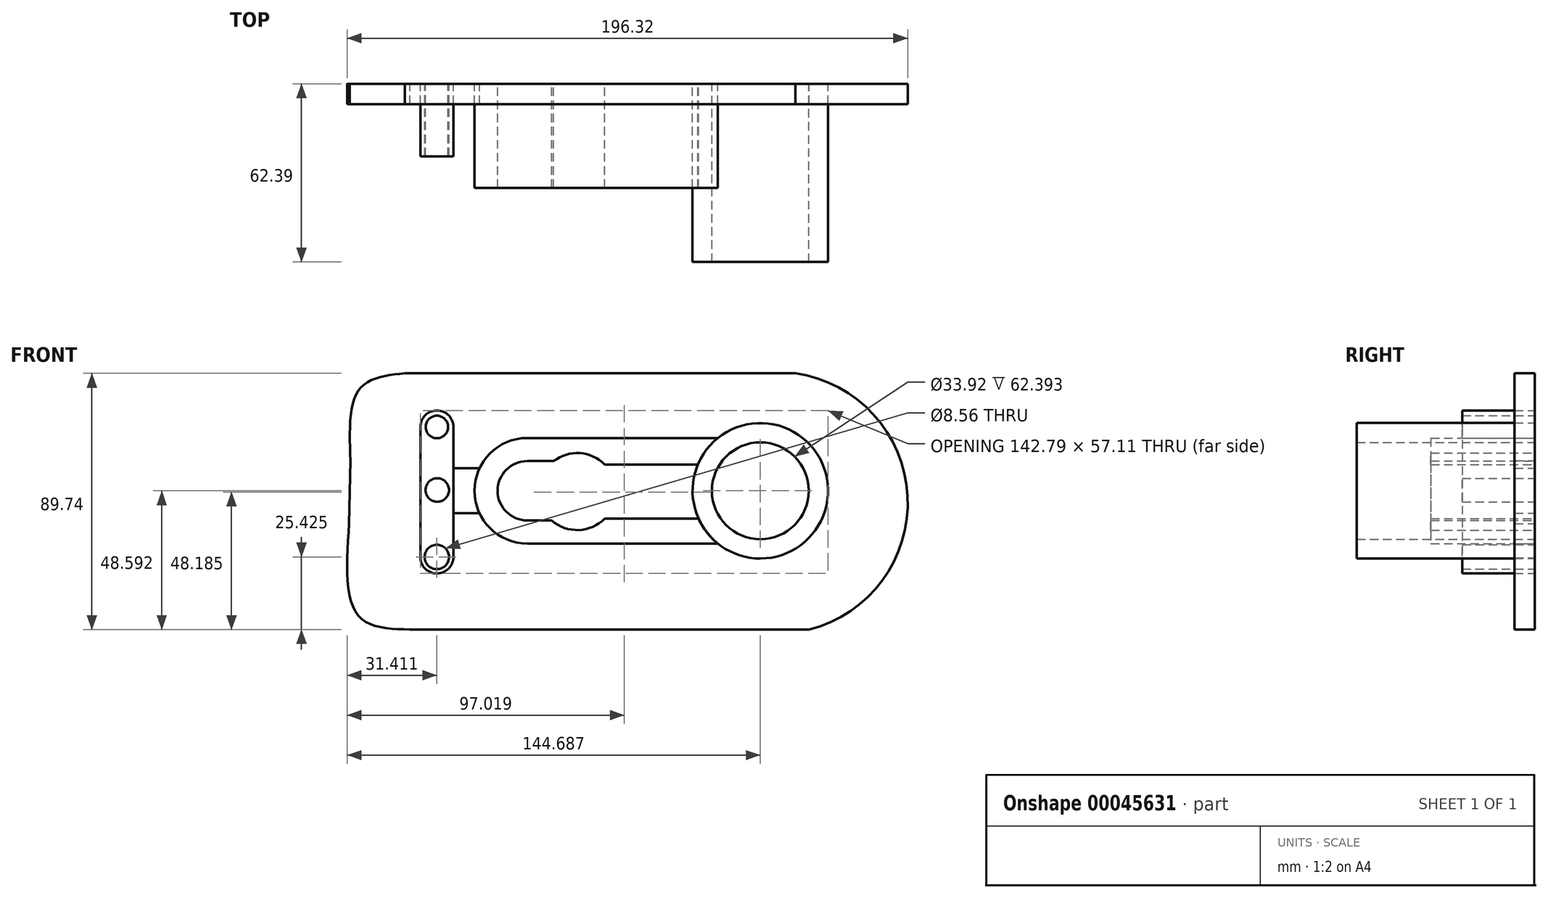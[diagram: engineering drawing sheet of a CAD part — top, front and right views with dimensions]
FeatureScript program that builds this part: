
annotation { "Feature Type Name" : "Feature", "Feature Type Description" : "" }
export const myFeature = defineFeature(function(context is Context, id is Id, definition is map)
    precondition{}
    {
        {
            var Q0;
            Q0=qCreatedBy(makeId("Front.planeOp"),FACE);
            var sketch = newSketch(context, id + "F0", { "sketchPlane" : qUnion([Q0])});
            skLineSegment(sketch, "E0", {"start": v(-64.59, 29) * mm, "end": v(-64.59, -16.8) * mm});
            skArc(sketch, "E1", {"start": v(-64.59, 29) * mm, "mid": v(-58.8, 34.79) * mm, "end": v(-53, 29) * mm});
            skLineSegment(sketch, "E2", {"start": v(-53, 29) * mm, "end": v(-53, -16.52) * mm});
            skArc(sketch, "E3", {"start": v(-53, -16.52) * mm, "mid": v(-58.66, -22.32) * mm, "end": v(-64.59, -16.8) * mm});
            skCircle(sketch, "E4", {"center": v(-58.8, 29) * mm, "radius": 3.93 * mm});
            skCircle(sketch, "E5", {"center": v(-58.8, -16.52) * mm, "radius": 4.28 * mm});
            skCircle(sketch, "E6", {"center": v(54.48, 6.64) * mm, "radius": 23.73 * mm});
            skCircle(sketch, "E7", {"center": v(54.48, 6.64) * mm, "radius": 16.96 * mm});
            skCircle(sketch, "E8", {"center": v(54.48, 6.64) * mm, "radius": 14.65 * mm});
            skLineSegment(sketch, "E9", {"start": v(39.6, 25.12) * mm, "end": v(-27.14, 25.12) * mm});
            skLineSegment(sketch, "E10", {"start": v(39.6, -11.84) * mm, "end": v(-27.14, -11.84) * mm});
            skCircle(sketch, "E11", {"center": v(-9.63, 6.37) * mm, "radius": 13.5 * mm});
            skCircle(sketch, "E12", {"center": v(-9.63, 6.37) * mm, "radius": 9.21 * mm});
            skCircle(sketch, "E13", {"center": v(-9.63, 6.37) * mm, "radius": 7.09 * mm});
            skArc(sketch, "E14", {"start": v(-27.14, 25.12) * mm, "mid": v(-45.62, 6.64) * mm, "end": v(-27.14, -11.84) * mm});
            skLineSegment(sketch, "E15", {"start": v(-17.9, 17.04) * mm, "end": v(-27.14, 17.04) * mm});
            skLineSegment(sketch, "E16", {"start": v(-18.55, -3.75) * mm, "end": v(-27.14, -3.75) * mm});
            skArc(sketch, "E17", {"start": v(-27.14, 17.04) * mm, "mid": v(-37.53, 6.64) * mm, "end": v(-27.14, -3.75) * mm});
            skLineSegment(sketch, "E18", {"start": v(-43.87, 14.51) * mm, "end": v(-53, 14.51) * mm});
            skLineSegment(sketch, "E19", {"start": v(-43.87, -1.23) * mm, "end": v(-53, -1.23) * mm});
            skCircle(sketch, "E20", {"center": v(-58.66, 6.91) * mm, "radius": 4.12 * mm});
            skArc(sketch, "E21", {"start": v(71.62, -41.95) * mm, "mid": v(106.05, 4.9) * mm, "end": v(66.79, 47.8) * mm});
            skLineSegment(sketch, "E22", {"start": v(66.79, 47.8) * mm, "end": v(-70, 47.8) * mm});
            skLineSegment(sketch, "E23", {"start": v(71.62, -41.95) * mm, "end": v(-68.22, -41.95) * mm});
            skFitSpline(sketch, "E24", {"points": [v(-70, 47.8) * mm, v(-85.76, 42.45) * mm, v(-89.06, 17.28) * mm], "startDerivative": vector(-41.77, -4.41) * mm, "endDerivative": vector(2.1, -54.84) * mm});
            skFitSpline(sketch, "E25", {"points": [v(-68.22, -41.95) * mm, v(-86.27, -37.12) * mm, v(-89.57, -4.84) * mm], "startDerivative": vector(-49.61, 1.36) * mm, "endDerivative": vector(4.43, 69.75) * mm});
            skLineSegment(sketch, "E26", {"start": v(-89.57, -4.84) * mm, "end": v(-89.06, 17.28) * mm});
            skLineSegment(sketch, "E27", {"start": v(0, 15.82) * mm, "end": v(32.6, 15.82) * mm});
            skLineSegment(sketch, "E28", {"start": v(32.6, 15.82) * mm, "end": v(0, 15.82) * mm});
            skLineSegment(sketch, "E29", {"start": v(0, -3.08) * mm, "end": v(32.83, -3.08) * mm});
            skLineSegment(sketch, "E30", {"start": v(32.83, -3.08) * mm, "end": v(0, -3.08) * mm});
            skSolve(sketch);
        }
        {
            var Q0;
            Q0=makeQuery(id+"F0.imprint","IMPRINT",FACE,{"disambiguationData":[TD([[makeQuery(id+"F0.imprint","IMPRINT",EDGE,{"derivedFrom":sQuery(id+"F0.wireOp",EDGE,"E0")}),1.0]])]});
            extrude(context, id + "F1", {"entities" : qUnion([Q0]), "depth" : 25.4 * mm});
        }
        {
            var Q0;
            Q0=makeQuery(id+"F0.imprint","IMPRINT",FACE,{"disambiguationData":[TD([[makeQuery(id+"F0.imprint","IMPRINT",EDGE,{"derivedFrom":sQuery(id+"F0.wireOp",EDGE,"E7")}),-1.0]])]});
            extrude(context, id + "F2", {"entities" : qUnion([Q0]), "depth" : 62.4 * mm});
        }
        {
            var Q0;
            {var subQ4=sQuery(id+"F0.wireOp",EDGE,"E9");Q0=makeQuery(id+"F0.imprint","IMPRINT",FACE,{"disambiguationData":[TD([[makeQuery(id+"F0.imprint","IMPRINT",EDGE,{"derivedFrom":subQ4}),1.0]])]});}
            extrude(context, id + "F3", {"entities" : qUnion([Q0]), "operationType" : NewBodyOperationType.ADD, "depth" : 36.43 * mm});
        }
        {
            var Q0;
            Q0=sQuery(id+"F0.wireOp",EDGE,"E11");
            extrude(context, id + "F4", {"bodyType" : ToolBodyType.SURFACE, "surfaceEntities" : qUnion([Q0]), "depth" : 41.03 * mm});
        }
        {
            var Q0;
            Q0=sQuery(id+"F0.wireOp",EDGE,"E12");
            extrude(context, id + "F5", {"bodyType" : ToolBodyType.SURFACE, "surfaceEntities" : qUnion([Q0]), "depth" : 36.55 * mm});
        }
        {
            var Q0;
            Q0=makeQuery(id+"F0.imprint","IMPRINT",FACE,{"disambiguationData":[TD([[makeQuery(id+"F0.imprint","IMPRINT",EDGE,{"derivedFrom":sQuery(id+"F0.wireOp",EDGE,"E0")}),-1.0]])]});
            extrude(context, id + "F6", {"entities" : qUnion([Q0]), "depth" : 7.1 * mm});
        }
    });
